# Revit family: LSRK
name_source: partatom
category: Lighting Fixtures
revit_build: Autodesk Revit 2013 (Build: 20130531_2115(x64)
units: mm (PartAtom-declared; Revit-internal decimal feet)

## types (1)
- LSRK-5W-35LW-FA-EDU
    Apparent Load = 5 VA
    Color Filter = 16777215
    Default Elevation = 48"
    Description = Linear Strip Retrofit Kit / LED
    Dimming Lamp Color Temperature Shift = Incandescent Lamp Curve
    Emit Shape Visible in Rendering = No
    Emit from Rectangle Length = 47"
    Emit from Rectangle Width = 2 1/2"
    Finish = Hubbell-White
    Glass = Hubbell-White Glass
    Lamp = LED
    Load Classification = Lighting
    Lumen Output = Low Watt
    Manufacturer = Columbia Lighting
    Manufacturer Fax = 866-898-1065
    Model = LSRK
    Mounting = Wall Mount
    Photometric Notes = More IES files download Photometric Web Link
    Photometric Web File = generic.ies
    Photometric Web Link = http://www.columbialighting.com
    Power Factor = 1
    Product Documentation Link = http://cdn.columbialighting.com
    Product Page URL = http://www.columbialighting.com
    Shielding = Frosted Acrylic Lens with Endcaps
    Tilt Angle = 90.00°
    URL = http://www.columbialighting.com
    Voltage = 120 V
    Warranty = Five year warranty
    Wattage Comments = Replaces outdated, non-efficient strip lighting with low wattage, high lumen solutions
    Watts = 5 W

## geometry (parser evidence)
native form markers: Blend x6, Sweep x1
no freeform markers — native parametric forms only
